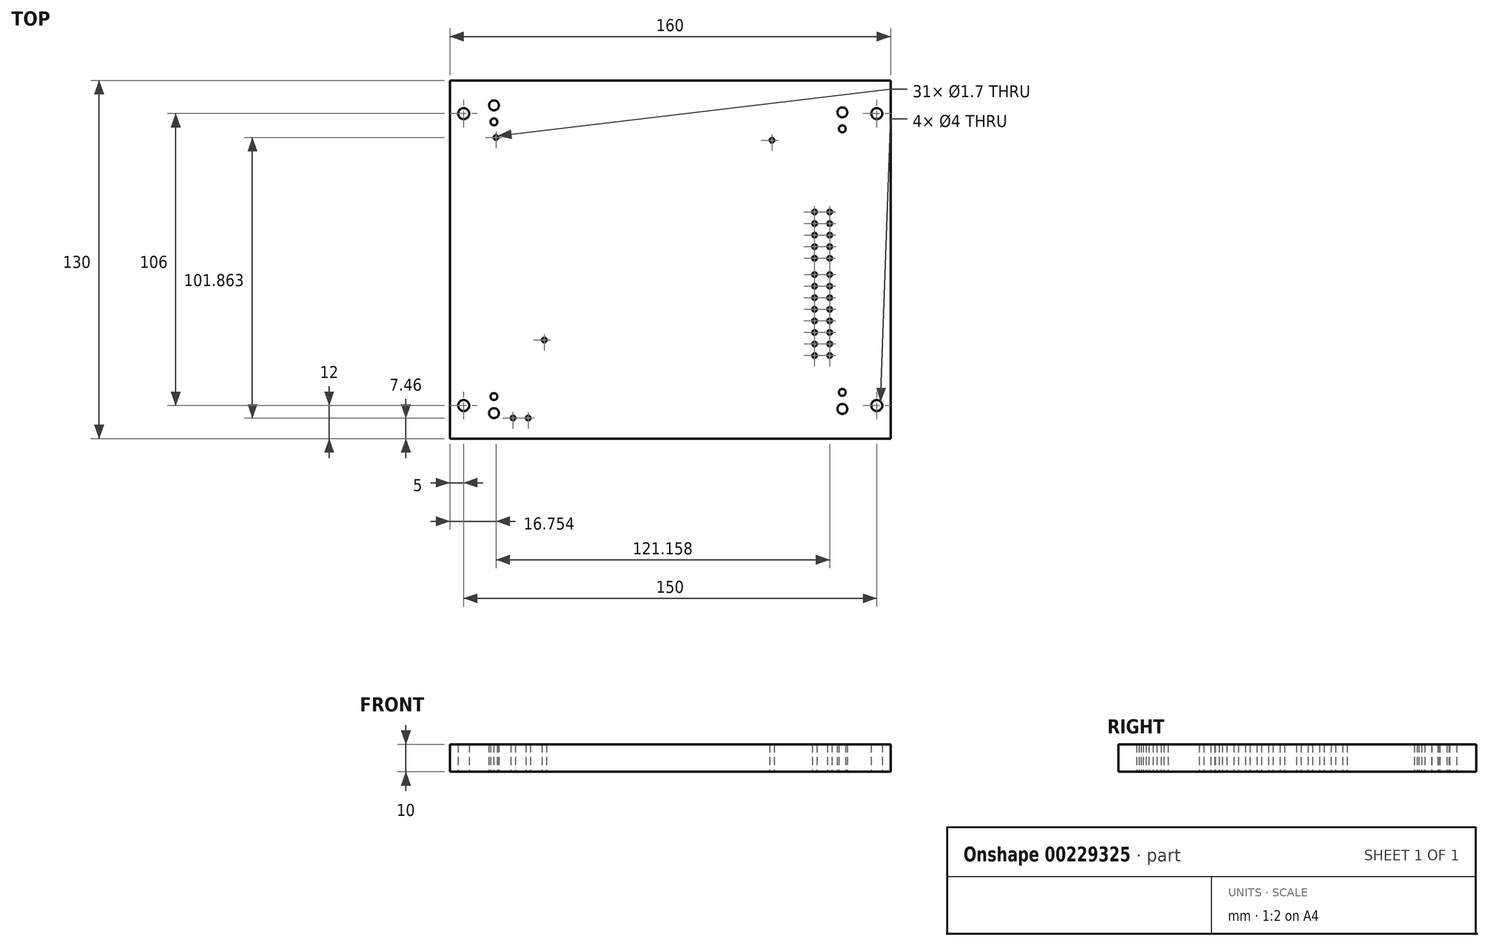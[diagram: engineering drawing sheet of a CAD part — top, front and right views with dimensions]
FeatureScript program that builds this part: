
annotation { "Feature Type Name" : "Feature", "Feature Type Description" : "" }
export const myFeature = defineFeature(function(context is Context, id is Id, definition is map)
    precondition{}
    {
        {
            var Q0;
            Q0=qCreatedBy(makeId("Top.planeOp"),FACE);
            var sketch = newSketch(context, id + "F0", { "sketchPlane" : qUnion([Q0])});
            skLineSegment(sketch, "E0.bottom", {"start": v(80, -65) * mm, "end": v(-80, -65) * mm});
            skLineSegment(sketch, "E0.top", {"start": v(80, 65) * mm, "end": v(-80, 65) * mm});
            skLineSegment(sketch, "E0.left", {"start": v(80, -65) * mm, "end": v(80, 65) * mm});
            skLineSegment(sketch, "E0.right", {"start": v(-80, -65) * mm, "end": v(-80, 65) * mm});
            skCircle(sketch, "E1", {"center": v(-75, -53) * mm, "radius": 2 * mm});
            skCircle(sketch, "E2.MirrorC", {"center": v(75, -53) * mm, "radius": 2 * mm});
            skCircle(sketch, "E3.MirrorC", {"center": v(-75, 53) * mm, "radius": 2 * mm});
            skCircle(sketch, "E4.MirrorC", {"center": v(75, 53) * mm, "radius": 2 * mm});
            skCircle(sketch, "E5", {"center": v(57.91, -34.86) * mm, "radius": 0.85 * mm});
            skCircle(sketch, "E6.0.1.0", {"center": v(57.91, -30.66) * mm, "radius": 0.85 * mm});
            skCircle(sketch, "E6.0.2.0", {"center": v(57.91, -26.46) * mm, "radius": 0.85 * mm});
            skCircle(sketch, "E6.0.3.0", {"center": v(57.91, -22.26) * mm, "radius": 0.85 * mm});
            skCircle(sketch, "E6.0.4.0", {"center": v(57.91, -18.06) * mm, "radius": 0.85 * mm});
            skCircle(sketch, "E6.0.5.0", {"center": v(57.91, -13.86) * mm, "radius": 0.85 * mm});
            skCircle(sketch, "E6.0.6.0", {"center": v(57.91, -9.66) * mm, "radius": 0.85 * mm});
            skCircle(sketch, "E6.0.7.0", {"center": v(57.91, -5.46) * mm, "radius": 0.85 * mm});
            skCircle(sketch, "E6.1.0.0", {"center": v(52.41, -34.86) * mm, "radius": 0.85 * mm});
            skCircle(sketch, "E6.1.1.0", {"center": v(52.41, -30.66) * mm, "radius": 0.85 * mm});
            skCircle(sketch, "E6.1.2.0", {"center": v(52.41, -26.46) * mm, "radius": 0.85 * mm});
            skCircle(sketch, "E6.1.3.0", {"center": v(52.41, -22.26) * mm, "radius": 0.85 * mm});
            skCircle(sketch, "E6.1.4.0", {"center": v(52.41, -18.06) * mm, "radius": 0.85 * mm});
            skCircle(sketch, "E6.1.5.0", {"center": v(52.41, -13.86) * mm, "radius": 0.85 * mm});
            skCircle(sketch, "E6.1.6.0", {"center": v(52.41, -9.66) * mm, "radius": 0.85 * mm});
            skCircle(sketch, "E6.1.7.0", {"center": v(52.41, -5.46) * mm, "radius": 0.85 * mm});
            skLineSegment(sketch, "E6.direction1", {"start": v(57.91, -34.86) * mm, "end": v(52.41, -34.86) * mm, "construction": true});
            skLineSegment(sketch, "E6.direction2", {"start": v(57.91, -34.86) * mm, "end": v(57.91, -30.66) * mm, "construction": true});
            skCircle(sketch, "E7", {"center": v(57.91, 0.47) * mm, "radius": 0.85 * mm});
            skCircle(sketch, "E8.0.1.0", {"center": v(57.91, 4.67) * mm, "radius": 0.85 * mm});
            skCircle(sketch, "E8.0.2.0", {"center": v(57.91, 8.87) * mm, "radius": 0.85 * mm});
            skCircle(sketch, "E8.0.3.0", {"center": v(57.91, 13.07) * mm, "radius": 0.85 * mm});
            skCircle(sketch, "E8.0.4.0", {"center": v(57.91, 17.27) * mm, "radius": 0.85 * mm});
            skCircle(sketch, "E8.1.0.0", {"center": v(52.41, 0.47) * mm, "radius": 0.85 * mm});
            skCircle(sketch, "E8.1.1.0", {"center": v(52.41, 4.67) * mm, "radius": 0.85 * mm});
            skCircle(sketch, "E8.1.2.0", {"center": v(52.41, 8.87) * mm, "radius": 0.85 * mm});
            skCircle(sketch, "E8.1.3.0", {"center": v(52.41, 13.07) * mm, "radius": 0.85 * mm});
            skCircle(sketch, "E8.1.4.0", {"center": v(52.41, 17.27) * mm, "radius": 0.85 * mm});
            skLineSegment(sketch, "E8.direction1", {"start": v(57.91, 0.47) * mm, "end": v(52.41, 0.47) * mm, "construction": true});
            skLineSegment(sketch, "E8.direction2", {"start": v(57.91, 0.47) * mm, "end": v(57.91, 4.67) * mm, "construction": true});
            skCircle(sketch, "E9", {"center": v(62.48, -54.23) * mm, "radius": 1.8 * mm});
            skCircle(sketch, "E10", {"center": v(62.48, 53.47) * mm, "radius": 1.8 * mm});
            skCircle(sketch, "E11", {"center": v(-64, 56) * mm, "radius": 1.8 * mm});
            skCircle(sketch, "E12", {"center": v(-64, -55.75) * mm, "radius": 1.8 * mm});
            skCircle(sketch, "E13", {"center": v(36.96, 43.3) * mm, "radius": 0.85 * mm});
            skCircle(sketch, "E14", {"center": v(-63.25, 44.32) * mm, "radius": 0.85 * mm});
            skCircle(sketch, "E15", {"center": v(-45.72, -29.21) * mm, "radius": 0.85 * mm});
            skCircle(sketch, "E16", {"center": v(-64, -55.75) * mm, "radius": 2.5 * mm, "construction": true});
            skCircle(sketch, "E17", {"center": v(-57.06, -57.54) * mm, "radius": 0.85 * mm});
            skCircle(sketch, "E18", {"center": v(-51.56, -57.54) * mm, "radius": 0.85 * mm});
            skCircle(sketch, "E19", {"center": v(-64, -49.75) * mm, "radius": 1.25 * mm});
            skCircle(sketch, "E20", {"center": v(62.48, -48.23) * mm, "radius": 1.25 * mm});
            skCircle(sketch, "E21", {"center": v(62.48, 47.47) * mm, "radius": 1.25 * mm});
            skCircle(sketch, "E22", {"center": v(-64, 50) * mm, "radius": 1.25 * mm});
            skCircle(sketch, "E23", {"center": v(62.48, 53.47) * mm, "radius": 2.5 * mm, "construction": true});
            skCircle(sketch, "E24", {"center": v(-64, 56) * mm, "radius": 2.5 * mm, "construction": true});
            skCircle(sketch, "E25", {"center": v(62.48, -54.23) * mm, "radius": 2.5 * mm, "construction": true});
            skSolve(sketch);
        }
        {
            var Q0;
            Q0 = qSketchRegion(id + "F0", true);
            extrude(context, id + "F1", {"entities" : qUnion([Q0]), "depth" : 10 * mm});
        }
    });
